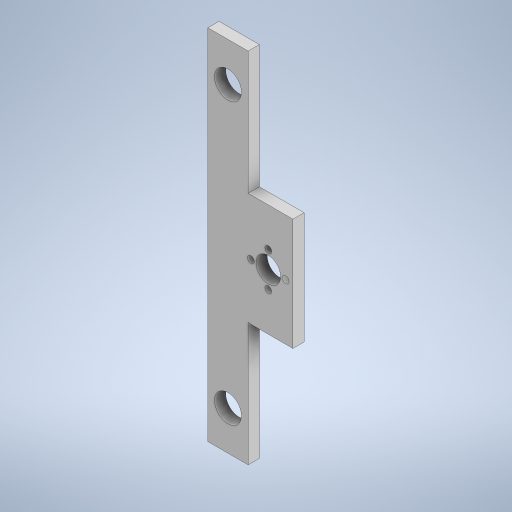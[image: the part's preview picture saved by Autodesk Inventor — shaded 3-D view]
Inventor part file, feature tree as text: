
AUTODESK INVENTOR PART (.ipt)
format: ipt  version: 2023.2 (Build 272271000, 271)  size: 414,208 bytes
history: native  units: mm
features: reference x4, other x3, sketch x2, extrude x1, hole x1
ambient origin geometry x8: Origin, YZ Plane, XZ Plane, XY Plane, X Axis, Y Axis, Z Axis, Center Point
bodies: Solid1 (feature_tree)
feature tree (11):
  extrude  "Extrusion1"  TaperAngle=90.0deg  [1 undecoded]
  hole  "Hole1"  [1 undecoded]
  sketch  "Sketch1"  dims[d0=160.0mm d1=90.0deg]
  sketch  "Sketch2"  dims[d2=18.0mm d3=12.0mm d4=12.0mm d5=125.113mm d6=20.0mm d7=50.0mm d8=55.0mm d11=5.0mm d12=0.0mm d15=11.0mm d16=9.0mm d17=17.4435mm d18=3.0mm d19=6.0mm d20=4.0mm d21=2.0mm d22=90.0deg d23=8.0mm d24=20.594885mm d25=9.0mm]
  reference  "Reference1"
  reference  "Reference2"
  reference  "Reference3"
  reference  "Reference4"
  parser-record x1  (decoder bookkeeping rows leaked as tree rows — omitted from the tree; the rows remain in map.json)
  other  "Main Assembly.iam"
  other  "ACME Brass Nut:1"
note: 2 required parameter values undecoded (feature->parameter linkage not recoverable at this tier; creation-order binding heuristic only, values carry confidence <= 0.55)
note: 1 file-system path scrubbed to <path> (originals preserved in map.json)
